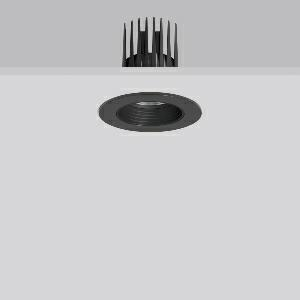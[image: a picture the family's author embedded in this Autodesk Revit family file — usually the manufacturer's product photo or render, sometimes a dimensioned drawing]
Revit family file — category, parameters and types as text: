
# Revit family: heledon_mini_e_901746_003_1_3d72
name_source: partatom
category: Lighting Fixtures
units: mm (PartAtom-declared; Revit-internal decimal feet)

## family parameters
Cut with Voids When Loaded = No
Host = Face
Light Source = No
Part Type = Normal
Room Calculation Point = No
Round Connector Dimension = Use Diameter
Shared = No

## types (1)
- HELEDON mini E (1 x LED Modul 940, 2450 lm, 4000)
    Apparent Load = 20 VA
    Approval mark = CE
    CIE Flux Codes = 80 99 100 100 100
    Color Rendering = 92
    Color Temperature = 4000
    Default Elevation = 1800 mm
    Description = Series: HELEDON mini
Round recessed downlight. Housing: die-cast aluminium, powder-coated. Black plastic ring and recessed LED to prevent glare from the side. Optical assembly with lens made of plastic (polycarbonate) for the best homogeneous light distribution - can be changed without tools. Best colour rendering index Ra>90. Suitable for Recessed ceiling mounting. Installation without tools thanks to spring fastening system. Including separate LED converter with connecting cable 600 mm.High quality converter without flickering and stroboscopic effect. Through-wiring box (5 pole) available as accessory. The following accessories can be mounted without use of tools: interchangeable lenses, decorative glasses, honeycomb louvre, clear and frosted diffusers, white interchangeable plastic ring. 
Colour: deep black, matt (RAL 9005)
Diameter: 124 mm
Height: 3 mm
Cut-out diameter: 114 mm
Recess height: 170 mm
Luminaire: recess height: 120 mm
Lamp: LED
Socket: without socket
Colour temperature: 4000K
Colour rendering index (CRI): 92
System power: 20 W
Rated luminous flux: 2450 lm
Luminous efficiency: 123 lm/W
Control gear: Regulated power supply
Protection class: II
Type of protection: IP 20
    Height = 0 mm  [stored 0 ft]
    Lamp = 1 x LED Modul 940
    Lamp Light Flux = 2450 lm
    Lamp count = 1
    Length = 124 mm  [stored 0.406824 ft]
    Lifetime = 50000 h
    Luminous efficacy = 123 lm/W
    Manufacturer = RZB
    ModVariant = No
    Model = 901746.003.1
    Mounting Place = Ceiling
    Mounting Type = Recessed
    Number of Poles = 1
    OnlyDefault = Yes
    Power Factor = 1
    Product Name = HELEDON mini E
    Product group = Recessed downlights
    ProductGroupID = 402
    Protection Class = Protection class II
    Protection Degree = IP 20
    RLX_Detail_Level = 1
    RLX_Emergency_Light_Flux = 0 lm
    RLX_Emergency_Type = 0
    RLX_Emergency_Type_DB = No
    RlxData = <blob elided: 126561 chars, md5=44bcf38e>
    Socket = socket
    Standby Power = 0 W
    System Light Flux = 2450 lm
    System Power = 20 W
    Type Comments = Product without accessories
    Type Image = 901656.003.jpg
    URL = http://relux.com
    VarID = ---
    Voltage = 230 V
    Voltage Range = 220-240 V
    Weight = 0.00 kg
    Width = 0 mm  [stored 0 ft]

note: [stored X ft] marks values corroborated as IEEE doubles in the binary element streams (Revit-internal decimal feet)

## geometry (parser evidence)
native form markers: Blend x4, Sweep x11
no freeform markers — native parametric forms only
